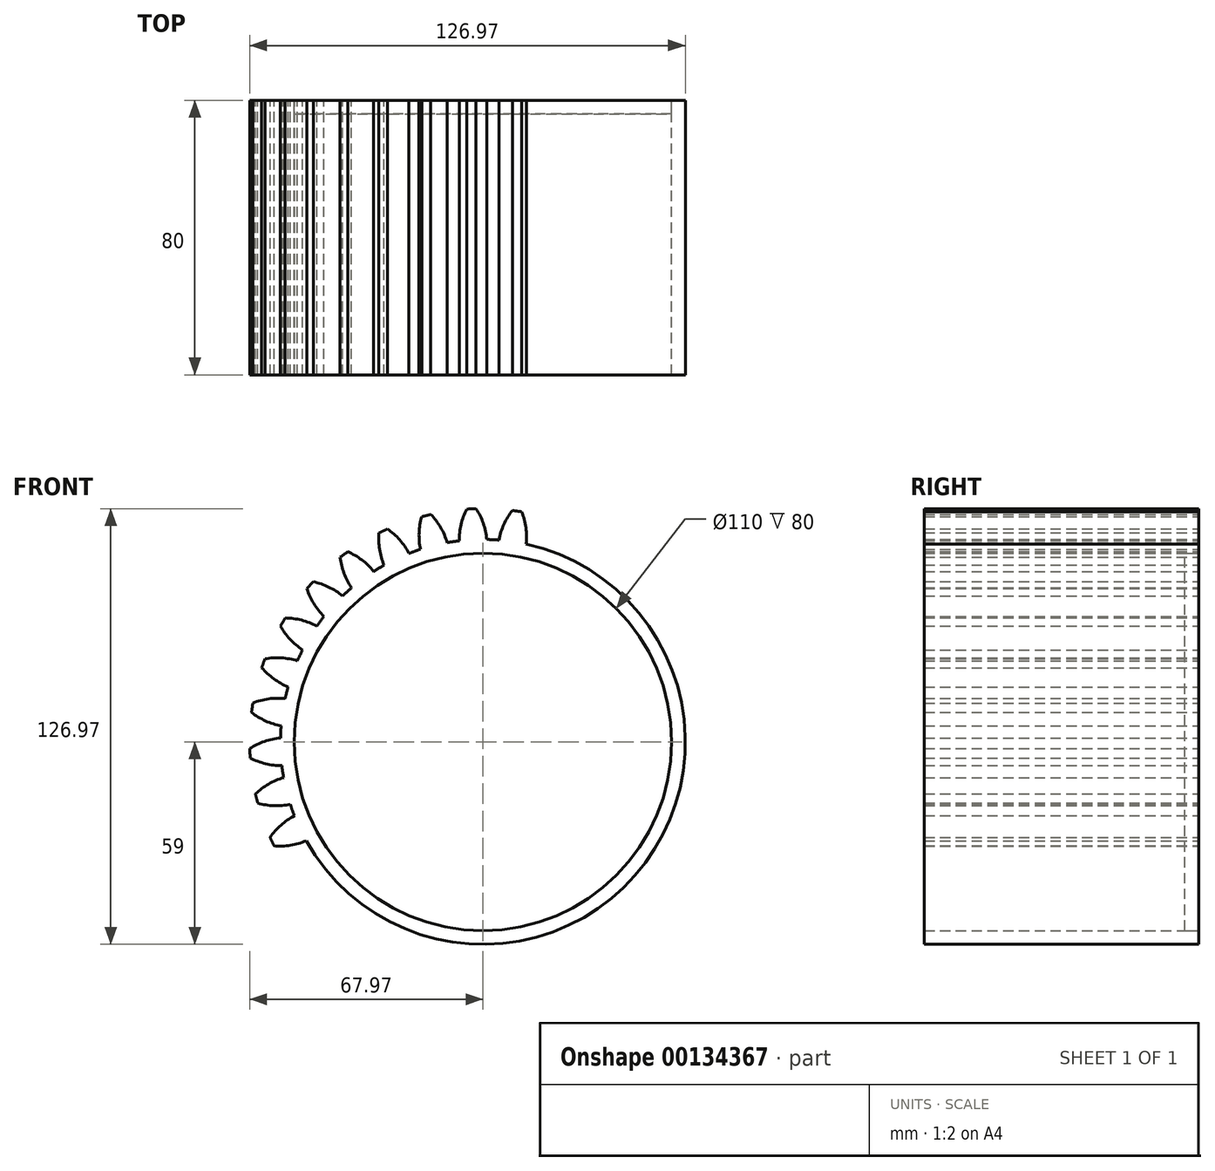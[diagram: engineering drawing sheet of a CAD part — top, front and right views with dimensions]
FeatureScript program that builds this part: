
annotation { "Feature Type Name" : "Feature", "Feature Type Description" : "" }
export const myFeature = defineFeature(function(context is Context, id is Id, definition is map)
    precondition{}
    {
        {
            var Q0;
            Q0=qCreatedBy(makeId("Front.planeOp"),FACE);
            var sketch = newSketch(context, id + "F0", { "sketchPlane" : qUnion([Q0])});
            skCircle(sketch, "E0", {"center": v(0, 0) * mm, "radius": 59 * mm});
            skCircle(sketch, "E1", {"center": v(0, 0) * mm, "radius": 64 * mm, "construction": true});
            skCircle(sketch, "E2", {"center": v(0, 0) * mm, "radius": 68 * mm, "construction": true});
            skLineSegment(sketch, "E3", {"start": v(0, 75.63) * mm, "end": v(0, 0) * mm, "construction": true});
            skLineSegment(sketch, "E4", {"start": v(0, 0) * mm, "end": v(-4.85, 98.7) * mm, "construction": true});
            skLineSegment(sketch, "E5", {"start": v(0, 64) * mm, "end": v(-49.24, 64) * mm, "construction": true});
            skLineSegment(sketch, "E6", {"start": v(0, 64) * mm, "end": v(-45.59, 47.4) * mm, "construction": true});
            skCircle(sketch, "E7", {"center": v(0, 0) * mm, "radius": 60.14 * mm, "construction": true});
            skCircle(sketch, "E8", {"center": v(0, 0) * mm, "radius": 55 * mm});
            skCircle(sketch, "E9", {"center": v(0, 64) * mm, "radius": 20 * mm, "construction": true});
            skCircle(sketch, "E10", {"center": v(-18.78, 57.13) * mm, "radius": 20 * mm, "construction": true});
            skArc(sketch, "E11", {"start": v(-1.97, 67.97) * mm, "mid": v(0.12, 63.67) * mm, "end": v(1.13, 58.99) * mm});
            skCircle(sketch, "E12.MirrorC", {"center": v(13.1, 58.7) * mm, "radius": 20 * mm, "construction": true});
            skArc(sketch, "E13.MirrorCS", {"start": v(-4.7, 67.84) * mm, "mid": v(-6.36, 63.35) * mm, "end": v(-6.9, 58.6) * mm});
            skArc(sketch, "E14", {"start": v(-4.7, 67.84) * mm, "mid": v(-3.34, 67.9) * mm, "end": v(-1.97, 67.97) * mm});
            skArc(sketch, "E15.1.0", {"start": v(-17.84, 65.62) * mm, "mid": v(-16.52, 65.94) * mm, "end": v(-15.2, 66.28) * mm});
            skArc(sketch, "E15.1.1", {"start": v(-17.84, 65.62) * mm, "mid": v(-18.6, 60.9) * mm, "end": v(-18.2, 56.12) * mm});
            skArc(sketch, "E15.1.2", {"start": v(-15.2, 66.28) * mm, "mid": v(-12.3, 62.47) * mm, "end": v(-10.4, 58.08) * mm});
            skArc(sketch, "E15.2.0", {"start": v(-30.3, 60.87) * mm, "mid": v(-29.06, 61.45) * mm, "end": v(-27.84, 62.04) * mm});
            skArc(sketch, "E15.2.1", {"start": v(-30.3, 60.87) * mm, "mid": v(-30.12, 56.1) * mm, "end": v(-28.8, 51.5) * mm});
            skArc(sketch, "E15.2.2", {"start": v(-27.84, 62.04) * mm, "mid": v(-24.25, 58.87) * mm, "end": v(-21.53, 54.93) * mm});
            skArc(sketch, "E15.3.0", {"start": v(-41.6, 53.8) * mm, "mid": v(-40.5, 54.6) * mm, "end": v(-39.4, 55.42) * mm});
            skArc(sketch, "E15.3.1", {"start": v(-41.6, 53.8) * mm, "mid": v(-40.48, 49.14) * mm, "end": v(-38.3, 44.88) * mm});
            skArc(sketch, "E15.3.2", {"start": v(-39.4, 55.42) * mm, "mid": v(-35.27, 53) * mm, "end": v(-31.83, 49.68) * mm});
            skArc(sketch, "E15.4.0", {"start": v(-51.29, 44.65) * mm, "mid": v(-50.37, 45.65) * mm, "end": v(-49.46, 46.67) * mm});
            skArc(sketch, "E15.4.1", {"start": v(-51.29, 44.65) * mm, "mid": v(-49.3, 40.3) * mm, "end": v(-46.32, 36.55) * mm});
            skArc(sketch, "E15.4.2", {"start": v(-49.46, 46.67) * mm, "mid": v(-44.94, 45.1) * mm, "end": v(-40.91, 42.51) * mm});
            skArc(sketch, "E15.5.0", {"start": v(-59.01, 33.78) * mm, "mid": v(-58.3, 34.95) * mm, "end": v(-57.61, 36.12) * mm});
            skArc(sketch, "E15.5.1", {"start": v(-59.01, 33.78) * mm, "mid": v(-56.2, 29.9) * mm, "end": v(-52.56, 26.81) * mm});
            skArc(sketch, "E15.5.2", {"start": v(-57.61, 36.12) * mm, "mid": v(-52.87, 35.47) * mm, "end": v(-48.42, 33.71) * mm});
            skArc(sketch, "E15.6.0", {"start": v(-64.47, 21.62) * mm, "mid": v(-64, 22.9) * mm, "end": v(-63.55, 24.19) * mm});
            skArc(sketch, "E15.6.1", {"start": v(-64.47, 21.62) * mm, "mid": v(-60.96, 18.37) * mm, "end": v(-56.78, 16.04) * mm});
            skArc(sketch, "E15.6.2", {"start": v(-63.55, 24.19) * mm, "mid": v(-58.77, 24.47) * mm, "end": v(-54.07, 23.62) * mm});
            skArc(sketch, "E15.7.0", {"start": v(-67.45, 8.63) * mm, "mid": v(-67.24, 9.97) * mm, "end": v(-67.05, 11.32) * mm});
            skArc(sketch, "E15.7.1", {"start": v(-67.45, 8.63) * mm, "mid": v(-63.37, 6.12) * mm, "end": v(-58.82, 4.66) * mm});
            skArc(sketch, "E15.7.2", {"start": v(-67.05, 11.32) * mm, "mid": v(-62.42, 12.54) * mm, "end": v(-57.64, 12.62) * mm});
            skArc(sketch, "E15.8.0", {"start": v(-67.84, -4.7) * mm, "mid": v(-67.9, -3.34) * mm, "end": v(-67.97, -1.97) * mm});
            skArc(sketch, "E15.8.1", {"start": v(-67.84, -4.7) * mm, "mid": v(-63.35, -6.36) * mm, "end": v(-58.6, -6.9) * mm});
            skArc(sketch, "E15.8.2", {"start": v(-67.97, -1.97) * mm, "mid": v(-63.67, 0.12) * mm, "end": v(-58.99, 1.13) * mm});
            skArc(sketch, "E15.9.0", {"start": v(-65.62, -17.84) * mm, "mid": v(-65.94, -16.52) * mm, "end": v(-66.28, -15.2) * mm});
            skArc(sketch, "E15.9.1", {"start": v(-65.62, -17.84) * mm, "mid": v(-60.9, -18.6) * mm, "end": v(-56.12, -18.2) * mm});
            skArc(sketch, "E15.9.2", {"start": v(-66.28, -15.2) * mm, "mid": v(-62.47, -12.3) * mm, "end": v(-58.08, -10.4) * mm});
            skArc(sketch, "E15.10.0", {"start": v(-60.87, -30.3) * mm, "mid": v(-61.45, -29.06) * mm, "end": v(-62.04, -27.84) * mm});
            skArc(sketch, "E15.10.1", {"start": v(-60.87, -30.3) * mm, "mid": v(-56.1, -30.12) * mm, "end": v(-51.5, -28.8) * mm});
            skArc(sketch, "E15.10.2", {"start": v(-62.04, -27.84) * mm, "mid": v(-58.87, -24.25) * mm, "end": v(-54.93, -21.53) * mm});
            skArc(sketch, "E15.31.0", {"start": v(8.63, 67.45) * mm, "mid": v(9.97, 67.24) * mm, "end": v(11.32, 67.05) * mm});
            skArc(sketch, "E15.31.1", {"start": v(8.63, 67.45) * mm, "mid": v(6.12, 63.37) * mm, "end": v(4.66, 58.82) * mm});
            skArc(sketch, "E15.31.2", {"start": v(11.32, 67.05) * mm, "mid": v(12.54, 62.42) * mm, "end": v(12.62, 57.64) * mm});
            skSolve(sketch);
        }
        {
            var Q0;
            {var subQ0=sQuery(id+"F0.wireOp",EDGE,"E0");var subQ1=makeQuery(id+"F0.imprint","INTERSECT",VERTEX,{"derivedFrom":[subQ0,sQuery(id+"F0.wireOp",EDGE,"loJ2GX96-QNjM-Q0Zs-GAVU-3QGzdKfrnFZ6")]});Q0=makeQuery(id+"F0.imprint","IMPRINT",FACE,{"disambiguationData":[TD([[makeQuery(id+"F0.imprint","IMPRINT",EDGE,{"disambiguationData":[TD([[subQ1,-1.0]])],"derivedFrom":subQ0}),1.0]])]});}
            extrude(context, id + "F1", {"entities" : qUnion([Q0]), "depth" : 80 * mm});
        }
        {
            var Q0;
            Q0=qSketchRegion(id+"F0",true);
            extrude(context, id + "F2", {"entities" : qUnion([Q0]), "operationType" : NewBodyOperationType.ADD, "depth" : 80 * mm});
        }
        {
            var Q0;
            Q0=makeQuery(id+"F0.imprint","IMPRINT",FACE,{"disambiguationData":[TD([[makeQuery(id+"F0.imprint","IMPRINT",EDGE,{"derivedFrom":sQuery(id+"F0.wireOp",EDGE,"E8")}),1.0]])]});
            extrude(context, id + "F3", {"entities" : qUnion([Q0]), "depth" : 4 * mm});
        }
    });
